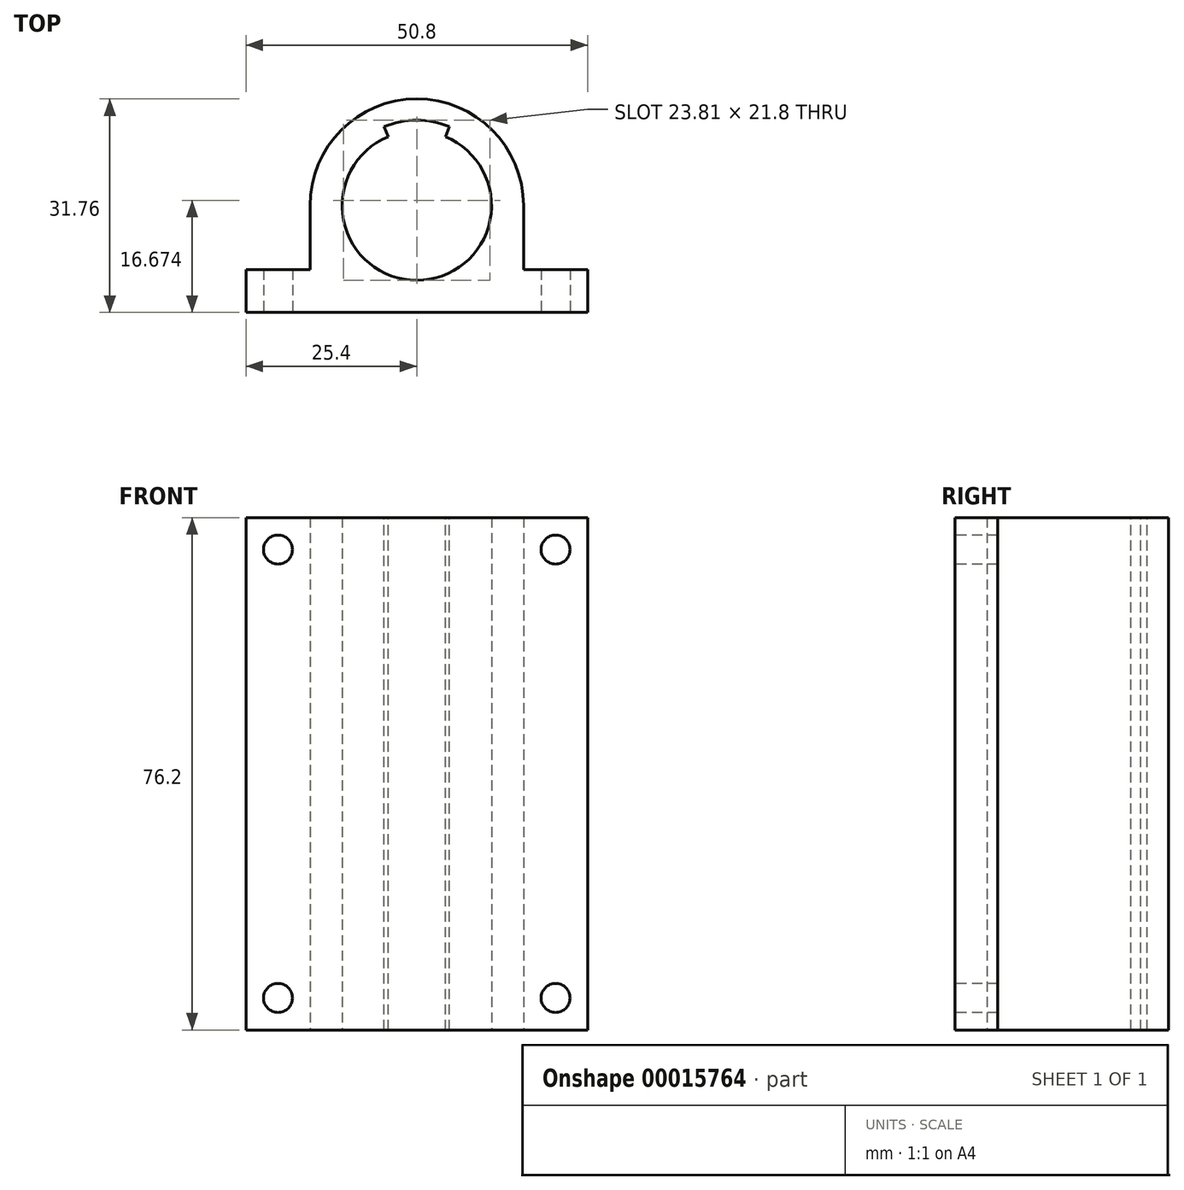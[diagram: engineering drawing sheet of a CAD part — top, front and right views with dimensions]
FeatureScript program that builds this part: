
annotation { "Feature Type Name" : "Feature", "Feature Type Description" : "" }
export const myFeature = defineFeature(function(context is Context, id is Id, definition is map)
    precondition{}
    {
        {
            var Q0;
            Q0=qCreatedBy(makeId("Top.planeOp"),FACE);
            var sketch = newSketch(context, id + "F0", { "sketchPlane" : qUnion([Q0])});
            skCircle(sketch, "E0", {"center": v(0, 0) * mm, "radius": 11.11 * mm});
            skArc(sketch, "E1", {"start": v(15.88, 0) * mm, "mid": v(0, 15.88) * mm, "end": v(-15.88, 0) * mm});
            skLineSegment(sketch, "E2.bottom", {"start": v(25.4, -15.87) * mm, "end": v(-25.4, -15.88) * mm});
            skLineSegment(sketch, "E2.left", {"start": v(25.4, -15.87) * mm, "end": v(25.4, -9.53) * mm});
            skLineSegment(sketch, "E2.right", {"start": v(-25.4, -15.88) * mm, "end": v(-25.4, -9.53) * mm});
            skLineSegment(sketch, "E3.bottom", {"start": v(15.88, 0) * mm, "end": v(-15.88, 0) * mm, "construction": true});
            skLineSegment(sketch, "E3.left", {"start": v(15.87, 0) * mm, "end": v(15.88, -9.53) * mm});
            skLineSegment(sketch, "E3.right", {"start": v(-15.88, 0) * mm, "end": v(-15.87, -9.53) * mm});
            skLineSegment(sketch, "E4", {"start": v(-25.4, -9.53) * mm, "end": v(-15.87, -9.53) * mm});
            skLineSegment(sketch, "E5", {"start": v(15.87, -9.52) * mm, "end": v(25.4, -9.52) * mm});
            skLineSegment(sketch, "E6", {"start": v(0, 0) * mm, "end": v(0, -15.88) * mm, "construction": true});
            skSolve(sketch);
        }
        {
            var Q0;
            Q0=qSketchRegion(id+"F0",true);
            extrude(context, id + "F1", {"entities" : qUnion([Q0]), "depth" : 76.2 * mm});
        }
        {
            var Q0;
            Q0=makeQuery(id+"F1.opExtrude","SWEPT_FACE",FACE,{"disambiguationData":[OSD([sQuery(id+"F0.wireOp",EDGE,"E2.bottom")])]});
            var sketch = newSketch(context, id + "F2", { "sketchPlane" : qUnion([Q0])});
            skLineSegment(sketch, "E7", {"start": v(0, 76.2) * mm, "end": v(0, 0) * mm, "construction": true});
            skLineSegment(sketch, "E8.bottom", {"start": v(-25.4, 76.2) * mm, "end": v(-20.64, 76.2) * mm, "construction": true});
            skLineSegment(sketch, "E8.top", {"start": v(-25.4, 71.44) * mm, "end": v(-20.64, 71.44) * mm, "construction": true});
            skLineSegment(sketch, "E8.left", {"start": v(-25.4, 76.2) * mm, "end": v(-25.4, 71.44) * mm, "construction": true});
            skLineSegment(sketch, "E8.right", {"start": v(-20.64, 76.2) * mm, "end": v(-20.64, 71.44) * mm, "construction": true});
            skLineSegment(sketch, "E9.bottom", {"start": v(-20.64, 71.44) * mm, "end": v(20.64, 71.44) * mm, "construction": true});
            skLineSegment(sketch, "E9.top", {"start": v(-20.64, 4.76) * mm, "end": v(20.64, 4.76) * mm, "construction": true});
            skLineSegment(sketch, "E9.left", {"start": v(-20.64, 71.44) * mm, "end": v(-20.64, 4.76) * mm, "construction": true});
            skLineSegment(sketch, "E9.right", {"start": v(20.64, 71.44) * mm, "end": v(20.64, 4.76) * mm, "construction": true});
            skPoint(sketch, "E9.middle", {"position": v(0, 38.1) * mm});
            skCircle(sketch, "E10", {"center": v(-20.64, 71.44) * mm, "radius": 2.15 * mm});
            skCircle(sketch, "E11", {"center": v(20.64, 71.44) * mm, "radius": 2.15 * mm});
            skCircle(sketch, "E12", {"center": v(20.64, 4.76) * mm, "radius": 2.15 * mm});
            skCircle(sketch, "E13", {"center": v(-20.64, 4.76) * mm, "radius": 2.15 * mm});
            skSolve(sketch);
        }
        {
            var Q0;
            Q0=qSketchRegion(id+"F2",true);
            var Q1;
            Q1=makeQuery(id+"F1.opExtrude","SWEPT_FACE",FACE,{"disambiguationData":[OSD([sQuery(id+"F0.wireOp",EDGE,"E5")])]});
            extrude(context, id + "F3", {"entities" : qUnion([Q0]), "operationType" : NewBodyOperationType.REMOVE, "endBound" : BoundingType.UP_TO_SURFACE, "oppositeDirection" : true, "endBoundEntityFace" : qUnion([Q1]), "depth" : 25.4 * mm});
        }
        {
            var Q0;
            Q0=makeQuery(id+"F1.opExtrude","CAP_FACE",FACE,{"disambiguationData":[OSD([sQuery(id+"F0.wireOp",EDGE,"E0"),sQuery(id+"F0.wireOp",EDGE,"E1"),sQuery(id+"F0.wireOp",EDGE,"E2.bottom"),sQuery(id+"F0.wireOp",EDGE,"E2.left"),sQuery(id+"F0.wireOp",EDGE,"E2.right"),sQuery(id+"F0.wireOp",EDGE,"E3.left"),sQuery(id+"F0.wireOp",EDGE,"E3.right"),sQuery(id+"F0.wireOp",EDGE,"E4"),sQuery(id+"F0.wireOp",EDGE,"E5")])],"isStart":false});
            var sketch = newSketch(context, id + "F4", { "sketchPlane" : qUnion([Q0])});
            skLineSegment(sketch, "E14", {"start": v(0, 0) * mm, "end": v(-4.25, 10.27) * mm, "construction": true});
            skLineSegment(sketch, "E15", {"start": v(0, 0) * mm, "end": v(4.25, 10.27) * mm, "construction": true});
            skArc(sketch, "E16", {"start": v(4.25, 10.27) * mm, "mid": v(0, 11.11) * mm, "end": v(-4.25, 10.27) * mm});
            skLineSegment(sketch, "E17", {"start": v(-4.25, 10.27) * mm, "end": v(-4.86, 11.73) * mm});
            skLineSegment(sketch, "E18", {"start": v(4.25, 10.27) * mm, "end": v(4.86, 11.73) * mm});
            skArc(sketch, "E19", {"start": v(4.86, 11.73) * mm, "mid": v(0, 12.7) * mm, "end": v(-4.86, 11.73) * mm});
            skLineSegment(sketch, "E20", {"start": v(0, 0) * mm, "end": v(0, 11.11) * mm, "construction": true});
            skSolve(sketch);
        }
        {
            var Q0;
            Q0 = qSketchRegion(id + "F4", true);
            var Q1;
            Q1=makeQuery(id+"F1.opExtrude","CAP_FACE",FACE,{"disambiguationData":[OSD([sQuery(id+"F0.wireOp",EDGE,"E0"),sQuery(id+"F0.wireOp",EDGE,"E1"),sQuery(id+"F0.wireOp",EDGE,"E2.bottom"),sQuery(id+"F0.wireOp",EDGE,"E2.left"),sQuery(id+"F0.wireOp",EDGE,"E2.right"),sQuery(id+"F0.wireOp",EDGE,"E3.left"),sQuery(id+"F0.wireOp",EDGE,"E3.right"),sQuery(id+"F0.wireOp",EDGE,"E4"),sQuery(id+"F0.wireOp",EDGE,"E5")])],"isStart":true});
            extrude(context, id + "F5", {"entities" : qUnion([Q0]), "operationType" : NewBodyOperationType.REMOVE, "endBound" : BoundingType.UP_TO_SURFACE, "oppositeDirection" : true, "endBoundEntityFace" : qUnion([Q1]), "depth" : 25.4 * mm});
        }
    });
